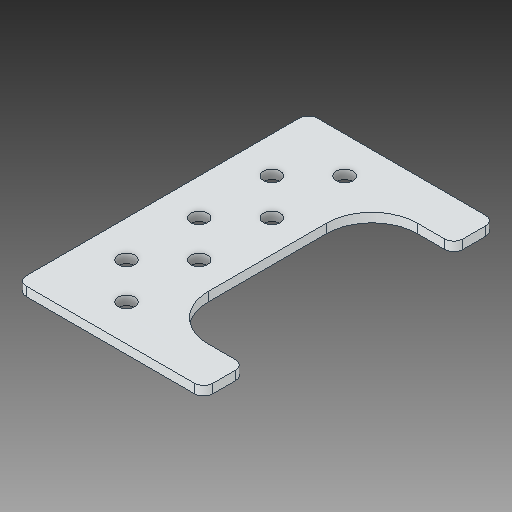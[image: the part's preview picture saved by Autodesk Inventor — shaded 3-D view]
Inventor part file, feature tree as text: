
AUTODESK INVENTOR PART (.ipt)
format: ipt  version: 2018 (Build 220112000, 112)  size: 137,216 bytes
history: native  units: in
note: dims shown in document units (in); Inventor stores cm internally (conversion verified against a paired STEP export)
features: fillet x1
ambient origin geometry x8: Origin, YZ Plane, XZ Plane, XY Plane, X Axis, Y Axis, Z Axis, Center Point
bodies: Solid1 (feature_tree)
feature tree (1):
  fillet  "Fillet3"  [1 undecoded]
note: 1 required parameter value undecoded (feature->parameter linkage not recoverable at this tier; creation-order binding heuristic only, values carry confidence <= 0.55)
